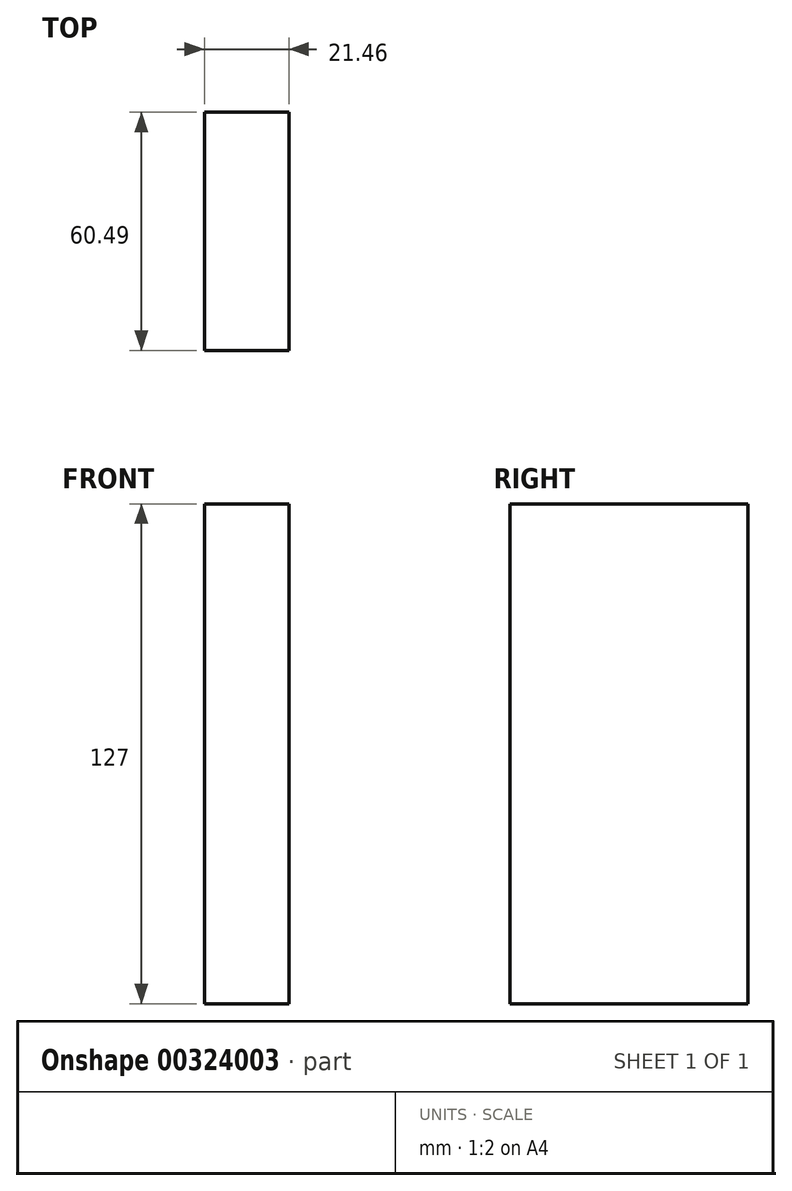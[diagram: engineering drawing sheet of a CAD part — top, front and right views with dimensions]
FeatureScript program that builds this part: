
annotation { "Feature Type Name" : "Feature", "Feature Type Description" : "" }
export const myFeature = defineFeature(function(context is Context, id is Id, definition is map)
    precondition{}
    {
        {
            var Q0;
            Q0=qCreatedBy(makeId("Top.planeOp"),FACE);
            var sketch = newSketch(context, id + "F0", { "sketchPlane" : qUnion([Q0])});
            skLineSegment(sketch, "E0.bottom", {"start": v(0, 0) * mm, "end": v(21.46, 0) * mm});
            skLineSegment(sketch, "E0.top", {"start": v(0, 60.49) * mm, "end": v(21.46, 60.49) * mm});
            skLineSegment(sketch, "E0.left", {"start": v(0, 0) * mm, "end": v(0, 60.49) * mm});
            skLineSegment(sketch, "E0.right", {"start": v(21.46, 0) * mm, "end": v(21.46, 60.49) * mm});
            skSolve(sketch);
        }
        {
            var Q0;
            Q0=makeQuery(id+"F0.imprint","IMPRINT",FACE,{"disambiguationData":[TD([[makeQuery(id+"F0.imprint","IMPRINT",EDGE,{"derivedFrom":sQuery(id+"F0.wireOp",EDGE,"E0.bottom")}),1.0]])]});
            extrude(context, id + "F1", {"entities" : qUnion([Q0]), "depth" : 127 * mm});
        }
    });
